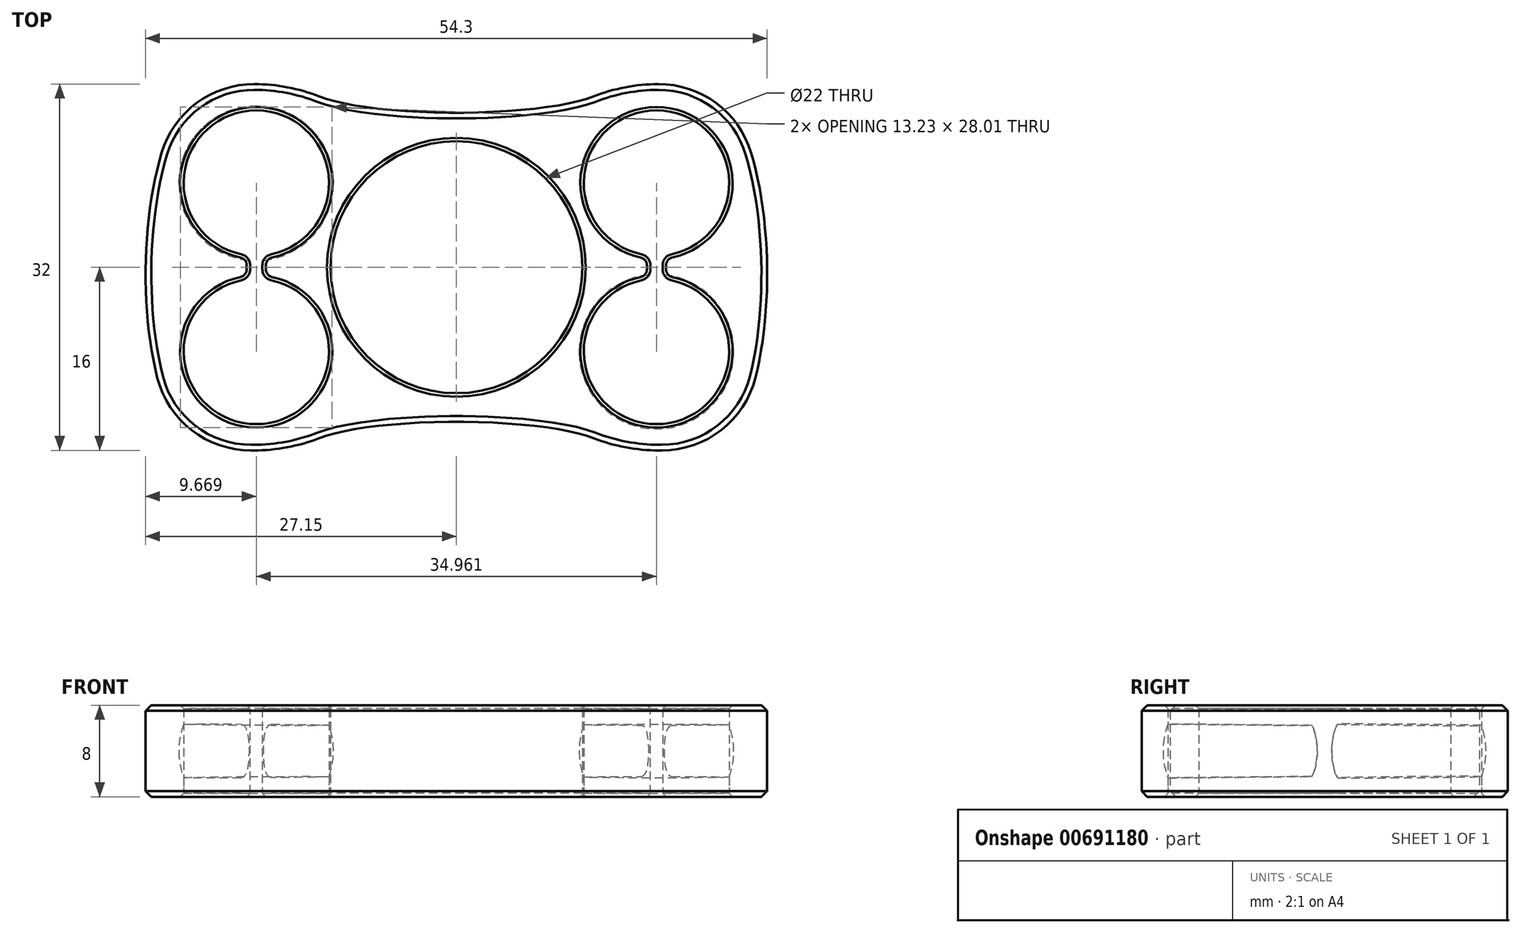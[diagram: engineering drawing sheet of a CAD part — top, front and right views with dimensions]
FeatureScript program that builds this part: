
annotation { "Feature Type Name" : "Feature", "Feature Type Description" : "" }
export const myFeature = defineFeature(function(context is Context, id is Id, definition is map)
    precondition{}
    {
        {
            var Q0;
            Q0=qCreatedBy(makeId("Top.planeOp"),FACE);
            var sketch = newSketch(context, id + "F0", { "sketchPlane" : qUnion([Q0])});
            skCircle(sketch, "E0", {"center": v(0, 0) * mm, "radius": 11 * mm});
            skLineSegment(sketch, "E1.bottom", {"start": v(22.5, -16) * mm, "end": v(13.27, -16) * mm});
            skLineSegment(sketch, "E1.top", {"start": v(21.78, 16) * mm, "end": v(13.27, 16) * mm});
            skArc(sketch, "E2", {"start": v(-16.95, 1.03) * mm, "mid": v(-17.48, 13.7) * mm, "end": v(-18.01, 1.03) * mm});
            skArc(sketch, "E3.MirrorC", {"start": v(16.95, 1.03) * mm, "mid": v(17.48, 13.7) * mm, "end": v(18.01, 1.03) * mm});
            skArc(sketch, "E4.MirrorC", {"start": v(-16.95, -1.03) * mm, "mid": v(-17.48, -13.7) * mm, "end": v(-18.01, -1.03) * mm});
            skArc(sketch, "E5.MirrorC", {"start": v(16.95, -1.03) * mm, "mid": v(17.48, -13.7) * mm, "end": v(18.01, -1.03) * mm});
            skPoint(sketch, "E1.right.end.orphan", {"position": v(-32.57, 16) * mm});
            skPoint(sketch, "E6.orphan", {"position": v(-32.7, -16) * mm});
            skEllipticalArc(sketch, "E7.trimOffspring", {});
            skPoint(sketch, "E8.center.orphan", {"position": v(-20.92, 0) * mm});
            skEllipticalArc(sketch, "E9.MirrorCS", {});
            skPoint(sketch, "E1.left.end.orphan", {"position": v(32.7, 16) * mm});
            skPoint(sketch, "E10.orphan", {"position": v(32.57, -16) * mm});
            skLineSegment(sketch, "E11.top", {"start": v(-16.95, 24.43) * mm, "end": v(-18.01, 24.43) * mm});
            skLineSegment(sketch, "E11.left", {"start": v(-16.95, -1.03) * mm, "end": v(-16.95, 1.03) * mm});
            skLineSegment(sketch, "E11.right", {"start": v(-18.01, -1.03) * mm, "end": v(-18.01, 1.03) * mm});
            skLineSegment(sketch, "E12.MirrorCS", {"start": v(16.95, -1.03) * mm, "end": v(16.95, 1.03) * mm});
            skLineSegment(sketch, "E13.MirrorCS", {"start": v(18.01, -1.03) * mm, "end": v(18.01, 1.03) * mm});
            skPoint(sketch, "E14.orphan", {"position": v(16.95, -9.72) * mm});
            skPoint(sketch, "E15.orphan", {"position": v(18.01, -9.72) * mm});
            skPoint(sketch, "E16.orphan", {"position": v(18.01, 13.68) * mm});
            skPoint(sketch, "E17.orphan", {"position": v(16.95, 13.68) * mm});
            skPoint(sketch, "E18.orphan", {"position": v(-16.95, 13.68) * mm});
            skPoint(sketch, "E19.orphan", {"position": v(-18.01, 13.68) * mm});
            skPoint(sketch, "E11.bottom.end.orphan", {"position": v(-18.01, -9.72) * mm});
            skPoint(sketch, "E11.bottom.start.orphan", {"position": v(-16.95, -9.72) * mm});
            skEllipticalArc(sketch, "E20", {});
            skLineSegment(sketch, "E21.trimOffspring", {"start": v(-13.27, 16) * mm, "end": v(-21.78, 16) * mm});
            skEllipticalArc(sketch, "E22.MirrorCS", {});
            skLineSegment(sketch, "E23.trimOffspring", {"start": v(-13.27, -16) * mm, "end": v(-22.5, -16) * mm});
            const initialGuessF0  = {"E7.trimOffspring": [-0.02127427164136021, -6.603079076637293e-05, 0.014211898565225475, 0.9998990058696787, 0.016182631006143217, 0.005870314556843559, 0.12454309048677038, 2.9717132687870937], "E9.MirrorCS": [0.02127427164136021, -6.603079076637294e-05, -0.014211898565225475, 0.9998990058696788, 0.016182631006143217, 0.005870314556843559, 3.3114720383924925, 6.158642216692816], "E20": [0, 0.016, -1, 0, 0.013273974880576135, 0.0025011457508088888, 6.283185307179585, 3.1415926535897927], "E22.MirrorCS": [0, -0.016, -1, 0, 0.013273974880576135, 0.0025011457508088888, 3.141592653589793, 0]};
            skSetInitialGuess(sketch, initialGuessF0);
            skSolve(sketch);
        }
        {
            var Q0;
            Q0=makeQuery(id+"F0.imprint","IMPRINT",FACE,{"disambiguationData":[TD([[makeQuery(id+"F0.imprint","IMPRINT",EDGE,{"derivedFrom":sQuery(id+"F0.wireOp",EDGE,"E0")}),-1.0]])]});
            extrude(context, id + "F1", {"entities" : qUnion([Q0]), "endBound" : BoundingType.SYMMETRIC, "depth" : 8 * mm, "offsetDistance" : 25 * mm});
        }
        {
            var Q0;
            Q0=makeQuery(id+"F1.opExtrude","SWEPT_EDGE",EDGE,{"disambiguationData":[OSD([sQuery(id+"F0.wireOp",EDGE,"E20"),sQuery(id+"F0.wireOp",EDGE,"E21.trimOffspring")])]});
            var Q1;
            Q1=makeQuery(id+"F1.opExtrude","SWEPT_EDGE",EDGE,{"disambiguationData":[OSD([sQuery(id+"F0.wireOp",EDGE,"E1.top"),sQuery(id+"F0.wireOp",EDGE,"E20")])]});
            var Q2;
            Q2=makeQuery(id+"F1.opExtrude","SWEPT_EDGE",EDGE,{"disambiguationData":[OSD([sQuery(id+"F0.wireOp",EDGE,"E1.bottom"),sQuery(id+"F0.wireOp",EDGE,"E22.MirrorCS")])]});
            var Q3;
            Q3=makeQuery(id+"F1.opExtrude","SWEPT_EDGE",EDGE,{"disambiguationData":[OSD([sQuery(id+"F0.wireOp",EDGE,"E22.MirrorCS"),sQuery(id+"F0.wireOp",EDGE,"E23.trimOffspring")])]});
            fillet(context, id + "F2", {"entities" : qUnion([Q0, Q1, Q2, Q3]), "radius" : 15.7 * mm, "tangentPropagation" : true, "allowEdgeOverflow" : false});
        }
        {
            var Q0;
            Q0=makeQuery(id+"F1.opExtrude","SWEPT_EDGE",EDGE,{"disambiguationData":[OSD([sQuery(id+"F0.wireOp",EDGE,"E7.trimOffspring"),sQuery(id+"F0.wireOp",EDGE,"E21.trimOffspring")])]});
            var Q1;
            Q1=makeQuery(id+"F1.opExtrude","SWEPT_EDGE",EDGE,{"disambiguationData":[OSD([sQuery(id+"F0.wireOp",EDGE,"E1.top"),sQuery(id+"F0.wireOp",EDGE,"E9.MirrorCS")])]});
            var Q2;
            Q2=makeQuery(id+"F1.opExtrude","SWEPT_EDGE",EDGE,{"disambiguationData":[OSD([sQuery(id+"F0.wireOp",EDGE,"E1.bottom"),sQuery(id+"F0.wireOp",EDGE,"E9.MirrorCS")])]});
            var Q3;
            Q3=makeQuery(id+"F1.opExtrude","SWEPT_EDGE",EDGE,{"disambiguationData":[OSD([sQuery(id+"F0.wireOp",EDGE,"E7.trimOffspring"),sQuery(id+"F0.wireOp",EDGE,"E23.trimOffspring")])]});
            fillet(context, id + "F3", {"entities" : qUnion([Q0, Q1, Q2, Q3]), "radius" : 8.43 * mm, "tangentPropagation" : true, "allowEdgeOverflow" : false});
        }
        {
            var Q0;
            Q0=makeQuery(id+"F1.opExtrude","CAP_EDGE",EDGE,{"disambiguationData":[OSD([sQuery(id+"F0.wireOp",EDGE,"E0")])],"isStart":false});
            var Q1;
            Q1=makeQuery(id+"F1.opExtrude","CAP_EDGE",EDGE,{"disambiguationData":[OSD([sQuery(id+"F0.wireOp",EDGE,"E0")])],"isStart":true});
            chamfer(context, id + "F4", {"entities" : qUnion([Q0, Q1]), "width" : .3 * mm, "tangentPropagation" : true});
        }
        {
            var Q0;
            Q0=makeQuery(id+"F1.opExtrude","SWEPT_EDGE",EDGE,{"disambiguationData":[OSD([sQuery(id+"F0.wireOp",EDGE,"E2"),sQuery(id+"F0.wireOp",EDGE,"E11.left")])]});
            var Q1;
            Q1=makeQuery(id+"F1.opExtrude","SWEPT_EDGE",EDGE,{"disambiguationData":[OSD([sQuery(id+"F0.wireOp",EDGE,"E2"),sQuery(id+"F0.wireOp",EDGE,"E11.right")])]});
            var Q2;
            Q2=makeQuery(id+"F1.opExtrude","SWEPT_EDGE",EDGE,{"disambiguationData":[OSD([sQuery(id+"F0.wireOp",EDGE,"E4.MirrorC"),sQuery(id+"F0.wireOp",EDGE,"E11.right")])]});
            var Q3;
            Q3=makeQuery(id+"F1.opExtrude","SWEPT_EDGE",EDGE,{"disambiguationData":[OSD([sQuery(id+"F0.wireOp",EDGE,"E4.MirrorC"),sQuery(id+"F0.wireOp",EDGE,"E11.left")])]});
            var Q4;
            Q4=makeQuery(id+"F1.opExtrude","SWEPT_EDGE",EDGE,{"disambiguationData":[OSD([sQuery(id+"F0.wireOp",EDGE,"E3.MirrorC"),sQuery(id+"F0.wireOp",EDGE,"E12.MirrorCS")])]});
            var Q5;
            Q5=makeQuery(id+"F1.opExtrude","SWEPT_EDGE",EDGE,{"disambiguationData":[OSD([sQuery(id+"F0.wireOp",EDGE,"E5.MirrorC"),sQuery(id+"F0.wireOp",EDGE,"E12.MirrorCS")])]});
            var Q6;
            Q6=makeQuery(id+"F1.opExtrude","SWEPT_EDGE",EDGE,{"disambiguationData":[OSD([sQuery(id+"F0.wireOp",EDGE,"E5.MirrorC"),sQuery(id+"F0.wireOp",EDGE,"E13.MirrorCS")])]});
            var Q7;
            Q7=makeQuery(id+"F1.opExtrude","SWEPT_EDGE",EDGE,{"disambiguationData":[OSD([sQuery(id+"F0.wireOp",EDGE,"E3.MirrorC"),sQuery(id+"F0.wireOp",EDGE,"E13.MirrorCS")])]});
            fillet(context, id + "F5", {"entities" : qUnion([Q0, Q1, Q2, Q3, Q4, Q5, Q6, Q7]), "radius" : 1 * mm, "tangentPropagation" : true, "allowEdgeOverflow" : false});
        }
        {
            var Q0;
            Q0=makeQuery(id+"F1.opExtrude","CAP_EDGE",EDGE,{"disambiguationData":[OSD([sQuery(id+"F0.wireOp",EDGE,"E22.MirrorCS")])],"isStart":false});
            var Q1;
            Q1=makeQuery(id+"F1.opExtrude","CAP_EDGE",EDGE,{"disambiguationData":[OSD([sQuery(id+"F0.wireOp",EDGE,"E22.MirrorCS")])],"isStart":true});
            chamfer(context, id + "F6", {"entities" : qUnion([Q0, Q1]), "width" : .5 * mm, "tangentPropagation" : true});
        }
        {
            var Q0;
            Q0=qCreatedBy(makeId("Top.planeOp"),FACE);
            var sketch = newSketch(context, id + "F7", { "sketchPlane" : qUnion([Q0])});
            skArc(sketch, "E24", {"start": v(-10.75, 7.33) * mm, "mid": v(-17.5, 14.08) * mm, "end": v(-24.25, 7.33) * mm});
            skLineSegment(sketch, "E25", {"start": v(-17.5, 7.33) * mm, "end": v(-9.86, 7.33) * mm});
            skLineSegment(sketch, "E26", {"start": v(-9.86, 7.33) * mm, "end": v(-10.75, 7.33) * mm});
            skLineSegment(sketch, "E27.trimOffspring", {"start": v(-17.5, 7.33) * mm, "end": v(-24.83, 7.33) * mm});
            skLineSegment(sketch, "E28.MirrorCS", {"start": v(17.5, 7.33) * mm, "end": v(9.86, 7.33) * mm});
            skLineSegment(sketch, "E29.MirrorCS", {"start": v(17.5, 7.33) * mm, "end": v(24.83, 7.33) * mm});
            skArc(sketch, "E30.MirrorC", {"start": v(10.75, 7.33) * mm, "mid": v(17.5, 14.08) * mm, "end": v(24.25, 7.33) * mm});
            skLineSegment(sketch, "E31.MirrorCS", {"start": v(-17.5, -7.33) * mm, "end": v(-9.86, -7.33) * mm});
            skLineSegment(sketch, "E32.MirrorCS", {"start": v(-17.5, -7.33) * mm, "end": v(-24.83, -7.33) * mm});
            skArc(sketch, "E33.MirrorC", {"start": v(-24.25, -7.33) * mm, "mid": v(-17.5, -0.58) * mm, "end": v(-10.75, -7.33) * mm});
            skArc(sketch, "E34.MirrorC", {"start": v(24.25, -7.33) * mm, "mid": v(17.5, -0.58) * mm, "end": v(10.75, -7.33) * mm});
            skLineSegment(sketch, "E35.MirrorCS", {"start": v(17.5, -7.33) * mm, "end": v(9.86, -7.33) * mm});
            skLineSegment(sketch, "E36.MirrorCS", {"start": v(17.5, -7.33) * mm, "end": v(24.83, -7.33) * mm});
            skSolve(sketch);
        }
        {
            var Q0;
            {var subQ0=sQuery(id+"F7.wireOp",EDGE,"E24");Q0=makeQuery(id+"F7.imprint","IMPRINT",FACE,{"disambiguationData":[TD([[makeQuery(id+"F7.imprint","IMPRINT",EDGE,{"derivedFrom":subQ0}),1.0]])]});}
            var Q1;
            {var subQ3=sQuery(id+"F7.wireOp",EDGE,"E30.MirrorC");Q1=makeQuery(id+"F7.imprint","IMPRINT",FACE,{"disambiguationData":[TD([[makeQuery(id+"F7.imprint","IMPRINT",EDGE,{"derivedFrom":subQ3}),-1.0]])]});}
            var Q2;
            Q2=sQuery(id+"F7.wireOp",EDGE,"E27.trimOffspring");
            revolve(context, id + "F8", {"operationType" : NewBodyOperationType.REMOVE, "entities" : qUnion([Q0, Q1]), "axis" : qUnion([Q2]), "revolveType" : RevolveType.FULL});
        }
        {
            var Q0;
            Q0=qCreatedBy(makeId("Top.planeOp"),FACE);
            var sketch = newSketch(context, id + "F9", { "sketchPlane" : qUnion([Q0])});
            skLineSegment(sketch, "E37.MirrorCS", {"start": v(-17.51, -7.38) * mm, "end": v(-9.88, -7.38) * mm});
            skLineSegment(sketch, "E38.MirrorCS", {"start": v(-17.51, -7.38) * mm, "end": v(-24.84, -7.38) * mm});
            skArc(sketch, "E39.MirrorC", {"start": v(-24.26, -7.38) * mm, "mid": v(-17.51, -0.63) * mm, "end": v(-10.76, -7.38) * mm});
            skArc(sketch, "E40.MirrorC", {"start": v(24.23, -7.38) * mm, "mid": v(17.48, -0.63) * mm, "end": v(10.73, -7.38) * mm});
            skLineSegment(sketch, "E41.MirrorCS", {"start": v(17.48, -7.38) * mm, "end": v(9.85, -7.38) * mm});
            skLineSegment(sketch, "E42.MirrorCS", {"start": v(17.48, -7.38) * mm, "end": v(24.81, -7.38) * mm});
            skSolve(sketch);
        }
        {
            var Q0;
            {var subQ3=sQuery(id+"F9.wireOp",EDGE,"E39.MirrorC");Q0=makeQuery(id+"F9.imprint","IMPRINT",FACE,{"disambiguationData":[TD([[makeQuery(id+"F9.imprint","IMPRINT",EDGE,{"derivedFrom":subQ3}),-1.0]])]});}
            var Q1;
            {var subQ0=sQuery(id+"F9.wireOp",EDGE,"E40.MirrorC");Q1=makeQuery(id+"F9.imprint","IMPRINT",FACE,{"disambiguationData":[TD([[makeQuery(id+"F9.imprint","IMPRINT",EDGE,{"derivedFrom":subQ0}),1.0]])]});}
            var Q2;
            Q2=sQuery(id+"F9.wireOp",EDGE,"E39.MirrorC");
            var Q3;
            Q3=sQuery(id+"F9.wireOp",EDGE,"E40.MirrorC");
            var Q4;
            Q4=sQuery(id+"F9.wireOp",EDGE,"E37.MirrorCS");
            revolve(context, id + "F10", {"operationType" : NewBodyOperationType.REMOVE, "entities" : qUnion([Q0, Q1]), "surfaceEntities" : qUnion([Q2, Q3]), "axis" : qUnion([Q4]), "revolveType" : RevolveType.FULL, "oppositeDirection" : true});
        }
        {
            var Q0;
            Q0=makeQuery(id+"F1.opExtrude","CAP_EDGE",EDGE,{"disambiguationData":[OSD([sQuery(id+"F0.wireOp",EDGE,"E4.MirrorC")])],"isStart":false});
            var Q1;
            {var subQ0=sQuery(id+"F0.wireOp",EDGE,"E11.left");var subQ1=sQuery(id+"F0.wireOp",EDGE,"E4.MirrorC");Q1=makeQuery(id+"F5.opFillet","BLEND_EDGE",EDGE,{"blendedFrom":[makeQuery(id+"F1.opExtrude","SWEPT_EDGE",EDGE,{"disambiguationData":[OSD([subQ1,subQ0])]}),makeQuery(id+"F1.opExtrude","CAP_FACE",FACE,{"disambiguationData":[OSD([sQuery(id+"F0.wireOp",EDGE,"E0"),sQuery(id+"F0.wireOp",EDGE,"E1.bottom"),sQuery(id+"F0.wireOp",EDGE,"E1.top"),sQuery(id+"F0.wireOp",EDGE,"E2"),sQuery(id+"F0.wireOp",EDGE,"E3.MirrorC"),subQ1,sQuery(id+"F0.wireOp",EDGE,"E5.MirrorC"),sQuery(id+"F0.wireOp",EDGE,"E7.trimOffspring"),sQuery(id+"F0.wireOp",EDGE,"E9.MirrorCS"),subQ0,sQuery(id+"F0.wireOp",EDGE,"E11.right"),sQuery(id+"F0.wireOp",EDGE,"E12.MirrorCS"),sQuery(id+"F0.wireOp",EDGE,"E13.MirrorCS"),sQuery(id+"F0.wireOp",EDGE,"E20"),sQuery(id+"F0.wireOp",EDGE,"E21.trimOffspring"),sQuery(id+"F0.wireOp",EDGE,"E22.MirrorCS"),sQuery(id+"F0.wireOp",EDGE,"E23.trimOffspring")])],"isStart":false})],"blendedInto":[makeQuery(id+"F1.opExtrude","CAP_FACE",FACE,{"disambiguationData":[OSD([sQuery(id+"F0.wireOp",EDGE,"E0"),sQuery(id+"F0.wireOp",EDGE,"E1.bottom"),sQuery(id+"F0.wireOp",EDGE,"E1.top"),sQuery(id+"F0.wireOp",EDGE,"E2"),sQuery(id+"F0.wireOp",EDGE,"E3.MirrorC"),subQ1,sQuery(id+"F0.wireOp",EDGE,"E5.MirrorC"),sQuery(id+"F0.wireOp",EDGE,"E7.trimOffspring"),sQuery(id+"F0.wireOp",EDGE,"E9.MirrorCS"),subQ0,sQuery(id+"F0.wireOp",EDGE,"E11.right"),sQuery(id+"F0.wireOp",EDGE,"E12.MirrorCS"),sQuery(id+"F0.wireOp",EDGE,"E13.MirrorCS"),sQuery(id+"F0.wireOp",EDGE,"E20"),sQuery(id+"F0.wireOp",EDGE,"E21.trimOffspring"),sQuery(id+"F0.wireOp",EDGE,"E22.MirrorCS"),sQuery(id+"F0.wireOp",EDGE,"E23.trimOffspring")])],"isStart":false})]});}
            var Q2;
            Q2=makeQuery(id+"F1.opExtrude","CAP_EDGE",EDGE,{"disambiguationData":[OSD([sQuery(id+"F0.wireOp",EDGE,"E11.left")])],"isStart":false});
            var Q3;
            {var subQ0=sQuery(id+"F0.wireOp",EDGE,"E11.left");var subQ1=sQuery(id+"F0.wireOp",EDGE,"E2");Q3=makeQuery(id+"F5.opFillet","BLEND_EDGE",EDGE,{"blendedFrom":[makeQuery(id+"F1.opExtrude","SWEPT_EDGE",EDGE,{"disambiguationData":[OSD([subQ1,subQ0])]}),makeQuery(id+"F1.opExtrude","CAP_FACE",FACE,{"disambiguationData":[OSD([sQuery(id+"F0.wireOp",EDGE,"E0"),sQuery(id+"F0.wireOp",EDGE,"E1.bottom"),sQuery(id+"F0.wireOp",EDGE,"E1.top"),subQ1,sQuery(id+"F0.wireOp",EDGE,"E3.MirrorC"),sQuery(id+"F0.wireOp",EDGE,"E4.MirrorC"),sQuery(id+"F0.wireOp",EDGE,"E5.MirrorC"),sQuery(id+"F0.wireOp",EDGE,"E7.trimOffspring"),sQuery(id+"F0.wireOp",EDGE,"E9.MirrorCS"),subQ0,sQuery(id+"F0.wireOp",EDGE,"E11.right"),sQuery(id+"F0.wireOp",EDGE,"E12.MirrorCS"),sQuery(id+"F0.wireOp",EDGE,"E13.MirrorCS"),sQuery(id+"F0.wireOp",EDGE,"E20"),sQuery(id+"F0.wireOp",EDGE,"E21.trimOffspring"),sQuery(id+"F0.wireOp",EDGE,"E22.MirrorCS"),sQuery(id+"F0.wireOp",EDGE,"E23.trimOffspring")])],"isStart":false})],"blendedInto":[makeQuery(id+"F1.opExtrude","CAP_FACE",FACE,{"disambiguationData":[OSD([sQuery(id+"F0.wireOp",EDGE,"E0"),sQuery(id+"F0.wireOp",EDGE,"E1.bottom"),sQuery(id+"F0.wireOp",EDGE,"E1.top"),subQ1,sQuery(id+"F0.wireOp",EDGE,"E3.MirrorC"),sQuery(id+"F0.wireOp",EDGE,"E4.MirrorC"),sQuery(id+"F0.wireOp",EDGE,"E5.MirrorC"),sQuery(id+"F0.wireOp",EDGE,"E7.trimOffspring"),sQuery(id+"F0.wireOp",EDGE,"E9.MirrorCS"),subQ0,sQuery(id+"F0.wireOp",EDGE,"E11.right"),sQuery(id+"F0.wireOp",EDGE,"E12.MirrorCS"),sQuery(id+"F0.wireOp",EDGE,"E13.MirrorCS"),sQuery(id+"F0.wireOp",EDGE,"E20"),sQuery(id+"F0.wireOp",EDGE,"E21.trimOffspring"),sQuery(id+"F0.wireOp",EDGE,"E22.MirrorCS"),sQuery(id+"F0.wireOp",EDGE,"E23.trimOffspring")])],"isStart":false})]});}
            var Q4;
            Q4=makeQuery(id+"F1.opExtrude","CAP_EDGE",EDGE,{"disambiguationData":[OSD([sQuery(id+"F0.wireOp",EDGE,"E2")])],"isStart":false});
            var Q5;
            {var subQ0=sQuery(id+"F0.wireOp",EDGE,"E11.right");var subQ1=sQuery(id+"F0.wireOp",EDGE,"E2");Q5=makeQuery(id+"F5.opFillet","BLEND_EDGE",EDGE,{"blendedFrom":[makeQuery(id+"F1.opExtrude","SWEPT_EDGE",EDGE,{"disambiguationData":[OSD([subQ1,subQ0])]}),makeQuery(id+"F1.opExtrude","CAP_FACE",FACE,{"disambiguationData":[OSD([sQuery(id+"F0.wireOp",EDGE,"E0"),sQuery(id+"F0.wireOp",EDGE,"E1.bottom"),sQuery(id+"F0.wireOp",EDGE,"E1.top"),subQ1,sQuery(id+"F0.wireOp",EDGE,"E3.MirrorC"),sQuery(id+"F0.wireOp",EDGE,"E4.MirrorC"),sQuery(id+"F0.wireOp",EDGE,"E5.MirrorC"),sQuery(id+"F0.wireOp",EDGE,"E7.trimOffspring"),sQuery(id+"F0.wireOp",EDGE,"E9.MirrorCS"),sQuery(id+"F0.wireOp",EDGE,"E11.left"),subQ0,sQuery(id+"F0.wireOp",EDGE,"E12.MirrorCS"),sQuery(id+"F0.wireOp",EDGE,"E13.MirrorCS"),sQuery(id+"F0.wireOp",EDGE,"E20"),sQuery(id+"F0.wireOp",EDGE,"E21.trimOffspring"),sQuery(id+"F0.wireOp",EDGE,"E22.MirrorCS"),sQuery(id+"F0.wireOp",EDGE,"E23.trimOffspring")])],"isStart":false})],"blendedInto":[makeQuery(id+"F1.opExtrude","CAP_FACE",FACE,{"disambiguationData":[OSD([sQuery(id+"F0.wireOp",EDGE,"E0"),sQuery(id+"F0.wireOp",EDGE,"E1.bottom"),sQuery(id+"F0.wireOp",EDGE,"E1.top"),subQ1,sQuery(id+"F0.wireOp",EDGE,"E3.MirrorC"),sQuery(id+"F0.wireOp",EDGE,"E4.MirrorC"),sQuery(id+"F0.wireOp",EDGE,"E5.MirrorC"),sQuery(id+"F0.wireOp",EDGE,"E7.trimOffspring"),sQuery(id+"F0.wireOp",EDGE,"E9.MirrorCS"),sQuery(id+"F0.wireOp",EDGE,"E11.left"),subQ0,sQuery(id+"F0.wireOp",EDGE,"E12.MirrorCS"),sQuery(id+"F0.wireOp",EDGE,"E13.MirrorCS"),sQuery(id+"F0.wireOp",EDGE,"E20"),sQuery(id+"F0.wireOp",EDGE,"E21.trimOffspring"),sQuery(id+"F0.wireOp",EDGE,"E22.MirrorCS"),sQuery(id+"F0.wireOp",EDGE,"E23.trimOffspring")])],"isStart":false})]});}
            var Q6;
            Q6=makeQuery(id+"F1.opExtrude","CAP_EDGE",EDGE,{"disambiguationData":[OSD([sQuery(id+"F0.wireOp",EDGE,"E11.right")])],"isStart":false});
            var Q7;
            {var subQ0=sQuery(id+"F0.wireOp",EDGE,"E11.right");var subQ1=sQuery(id+"F0.wireOp",EDGE,"E4.MirrorC");Q7=makeQuery(id+"F5.opFillet","BLEND_EDGE",EDGE,{"blendedFrom":[makeQuery(id+"F1.opExtrude","SWEPT_EDGE",EDGE,{"disambiguationData":[OSD([subQ1,subQ0])]}),makeQuery(id+"F1.opExtrude","CAP_FACE",FACE,{"disambiguationData":[OSD([sQuery(id+"F0.wireOp",EDGE,"E0"),sQuery(id+"F0.wireOp",EDGE,"E1.bottom"),sQuery(id+"F0.wireOp",EDGE,"E1.top"),sQuery(id+"F0.wireOp",EDGE,"E2"),sQuery(id+"F0.wireOp",EDGE,"E3.MirrorC"),subQ1,sQuery(id+"F0.wireOp",EDGE,"E5.MirrorC"),sQuery(id+"F0.wireOp",EDGE,"E7.trimOffspring"),sQuery(id+"F0.wireOp",EDGE,"E9.MirrorCS"),sQuery(id+"F0.wireOp",EDGE,"E11.left"),subQ0,sQuery(id+"F0.wireOp",EDGE,"E12.MirrorCS"),sQuery(id+"F0.wireOp",EDGE,"E13.MirrorCS"),sQuery(id+"F0.wireOp",EDGE,"E20"),sQuery(id+"F0.wireOp",EDGE,"E21.trimOffspring"),sQuery(id+"F0.wireOp",EDGE,"E22.MirrorCS"),sQuery(id+"F0.wireOp",EDGE,"E23.trimOffspring")])],"isStart":false})],"blendedInto":[makeQuery(id+"F1.opExtrude","CAP_FACE",FACE,{"disambiguationData":[OSD([sQuery(id+"F0.wireOp",EDGE,"E0"),sQuery(id+"F0.wireOp",EDGE,"E1.bottom"),sQuery(id+"F0.wireOp",EDGE,"E1.top"),sQuery(id+"F0.wireOp",EDGE,"E2"),sQuery(id+"F0.wireOp",EDGE,"E3.MirrorC"),subQ1,sQuery(id+"F0.wireOp",EDGE,"E5.MirrorC"),sQuery(id+"F0.wireOp",EDGE,"E7.trimOffspring"),sQuery(id+"F0.wireOp",EDGE,"E9.MirrorCS"),sQuery(id+"F0.wireOp",EDGE,"E11.left"),subQ0,sQuery(id+"F0.wireOp",EDGE,"E12.MirrorCS"),sQuery(id+"F0.wireOp",EDGE,"E13.MirrorCS"),sQuery(id+"F0.wireOp",EDGE,"E20"),sQuery(id+"F0.wireOp",EDGE,"E21.trimOffspring"),sQuery(id+"F0.wireOp",EDGE,"E22.MirrorCS"),sQuery(id+"F0.wireOp",EDGE,"E23.trimOffspring")])],"isStart":false})]});}
            var Q8;
            Q8=makeQuery(id+"F1.opExtrude","CAP_EDGE",EDGE,{"disambiguationData":[OSD([sQuery(id+"F0.wireOp",EDGE,"E4.MirrorC")])],"isStart":true});
            var Q9;
            Q9=makeQuery(id+"F1.opExtrude","CAP_EDGE",EDGE,{"disambiguationData":[OSD([sQuery(id+"F0.wireOp",EDGE,"E3.MirrorC")])],"isStart":true});
            var Q10;
            Q10=makeQuery(id+"F1.opExtrude","CAP_EDGE",EDGE,{"disambiguationData":[OSD([sQuery(id+"F0.wireOp",EDGE,"E5.MirrorC")])],"isStart":false});
            chamfer(context, id + "F11", {"entities" : qUnion([Q0, Q1, Q2, Q3, Q4, Q5, Q6, Q7, Q8, Q9, Q10]), "width" : .3 * mm, "tangentPropagation" : true});
        }
    });
